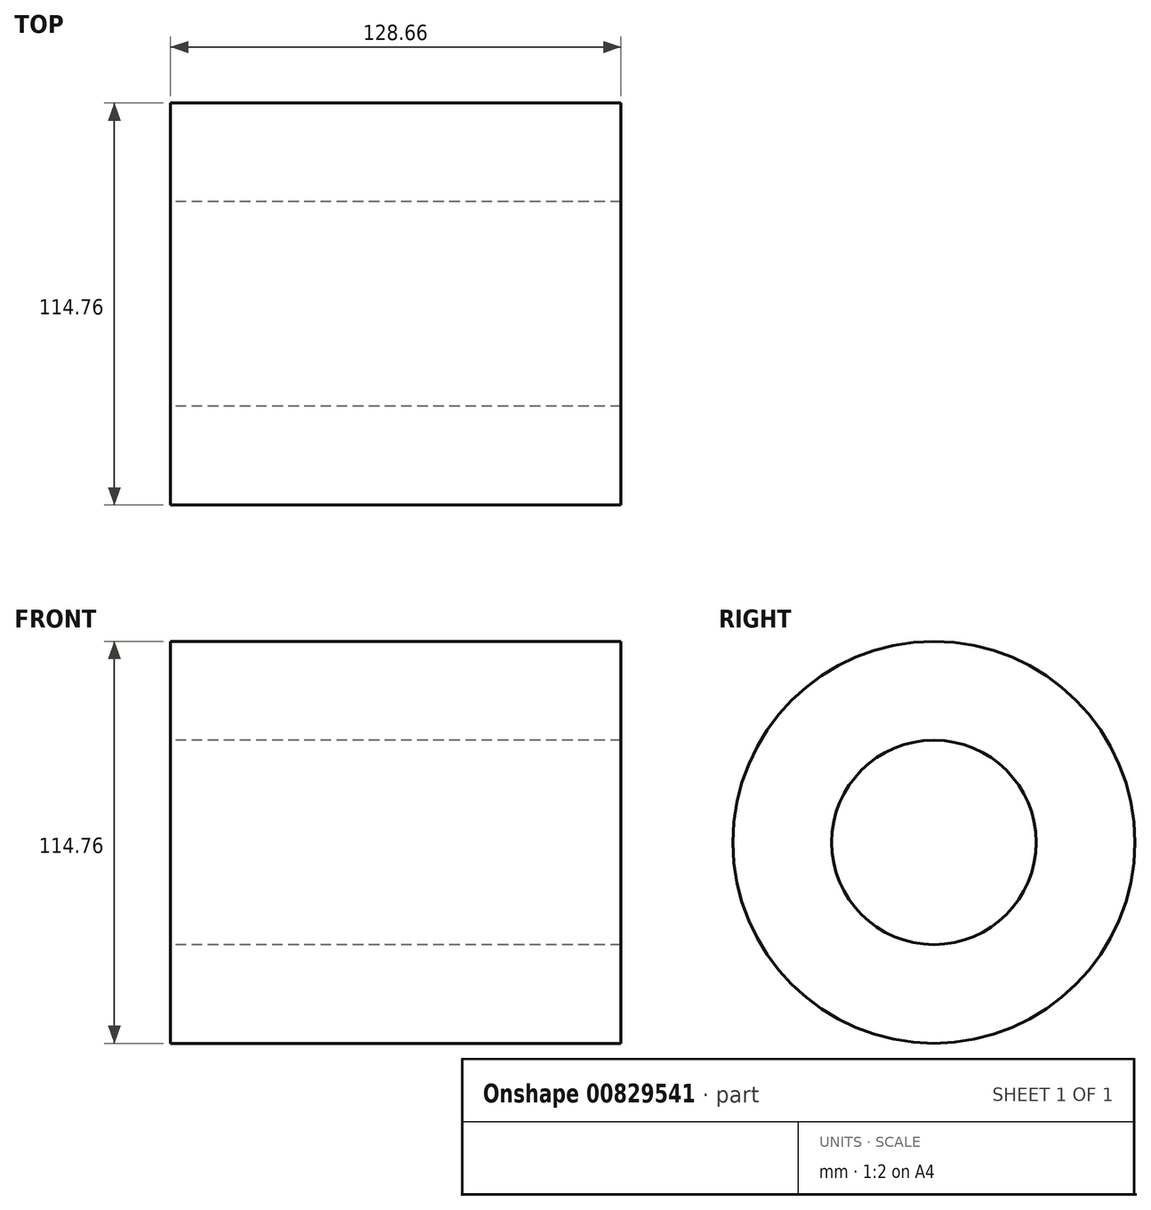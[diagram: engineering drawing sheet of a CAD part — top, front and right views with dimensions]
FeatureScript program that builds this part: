
annotation { "Feature Type Name" : "Feature", "Feature Type Description" : "" }
export const myFeature = defineFeature(function(context is Context, id is Id, definition is map)
    precondition{}
    {
        {
            var Q0;
            Q0=qCreatedBy(makeId("Right.planeOp"),FACE);
            var sketch = newSketch(context, id + "F0", { "sketchPlane" : qUnion([Q0])});
            skCircle(sketch, "E0", {"center": v(0, 0) * mm, "radius": 57.38 * mm});
            skSolve(sketch);
        }
        {
            var Q0;
            Q0=qCreatedBy(makeId("Right.planeOp"),FACE);
            var sketch = newSketch(context, id + "F1", { "sketchPlane" : qUnion([Q0])});
            skCircle(sketch, "E1", {"center": v(0, 0) * mm, "radius": 29.2 * mm});
            skSolve(sketch);
        }
        {
            var Q0;
            Q0 = qSketchRegion(id + "F1", true);
            var Q1;
            Q1=makeQuery(id+"F0.imprint","IMPRINT",FACE,{"disambiguationData":[TD([[makeQuery(id+"F0.imprint","IMPRINT",EDGE,{"derivedFrom":sQuery(id+"F0.wireOp",EDGE,"E0")}),1.0]])]});
            extrude(context, id + "F2", {"entities" : qUnion([Q0, Q1]), "depth" : 128.66 * mm, "offsetDistance" : 25.4 * mm});
        }
    });
